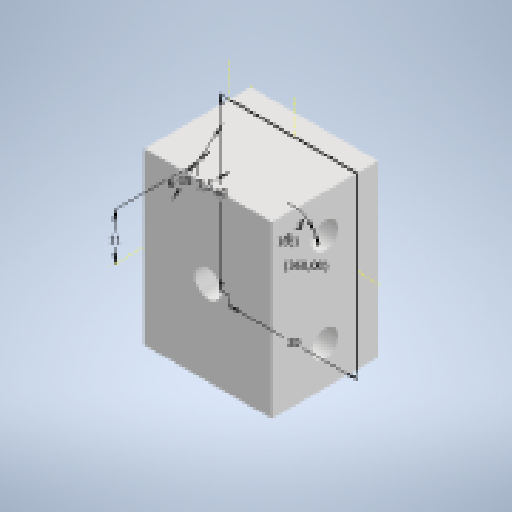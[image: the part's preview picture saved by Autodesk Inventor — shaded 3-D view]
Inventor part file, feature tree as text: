
AUTODESK INVENTOR PART (.ipt)
format: ipt  version: 2024.2 (Build 282272000, 272)  size: 269,312 bytes
history: native  units: mm
features: extrude x3, hole x3, sketch x2, other x1, fillet x1
ambient origin geometry x8: Origin, YZ Plane, XZ Plane, XY Plane, X Axis, Y Axis, Z Axis, Center Point
bodies: Body1 (feature_tree)
feature tree (10):
  other  "Bryła1"
  sketch  "Szkic1"
  extrude  "Wyciągnięcie proste1"  Depth=6.0mm
  extrude  "Wyciągnięcie proste2"  Depth=10.1mm
  fillet  "Zaokrąglenie1"  Radius=30.0mm
  sketch  "Szkic2"
  extrude  "Wyciągnięcie proste3"  Depth=40.0mm
  hole  "Otwór1"  [1 undecoded]
  hole  "Otwór2"  [1 undecoded]
  hole  "Otwór3"  [1 undecoded]
note: 3 required parameter values undecoded (feature->parameter linkage not recoverable at this tier; creation-order binding heuristic only, values carry confidence <= 0.55)
